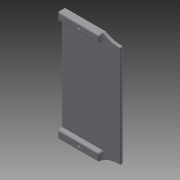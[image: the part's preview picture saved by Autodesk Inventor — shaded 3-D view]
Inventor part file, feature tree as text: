
AUTODESK INVENTOR PART (.ipt)
format: ipt  version: 2015 (Build 190159000, 159)  size: 160,768 bytes
history: native  units: mm
features: fillet x5, extrude x2, sketch x1
ambient origin geometry x8: Origin, YZ Plane, XZ Plane, XY Plane, X Axis, Y Axis, Z Axis, Center Point
bodies: Solid1 (feature_tree)
feature tree (8):
  sketch  "Sketch1"  dims[d4=10.0mm d5=10.0mm d8=32.2mm d9=32.2mm d14=3.0mm d15=3.0mm d16=3.0mm d17=0.0mm d18=5.0mm d19=0.0mm d20=2.0mm d21=2.0mm d22=1.0mm d23=1.0mm d24=1.0mm]
  extrude  "Extrusion1"  Depth=10.0mm
  extrude  "Extrusion2"  Depth=1.0mm
  fillet  "Fillet1"  Radius=32.2mm
  fillet  "Fillet2"  Radius=3.0mm
  fillet  "Fillet3"  Radius=3.0mm
  fillet  "Fillet4"  Radius=3.0mm
  fillet  "Fillet5"  Radius=5.0mm
